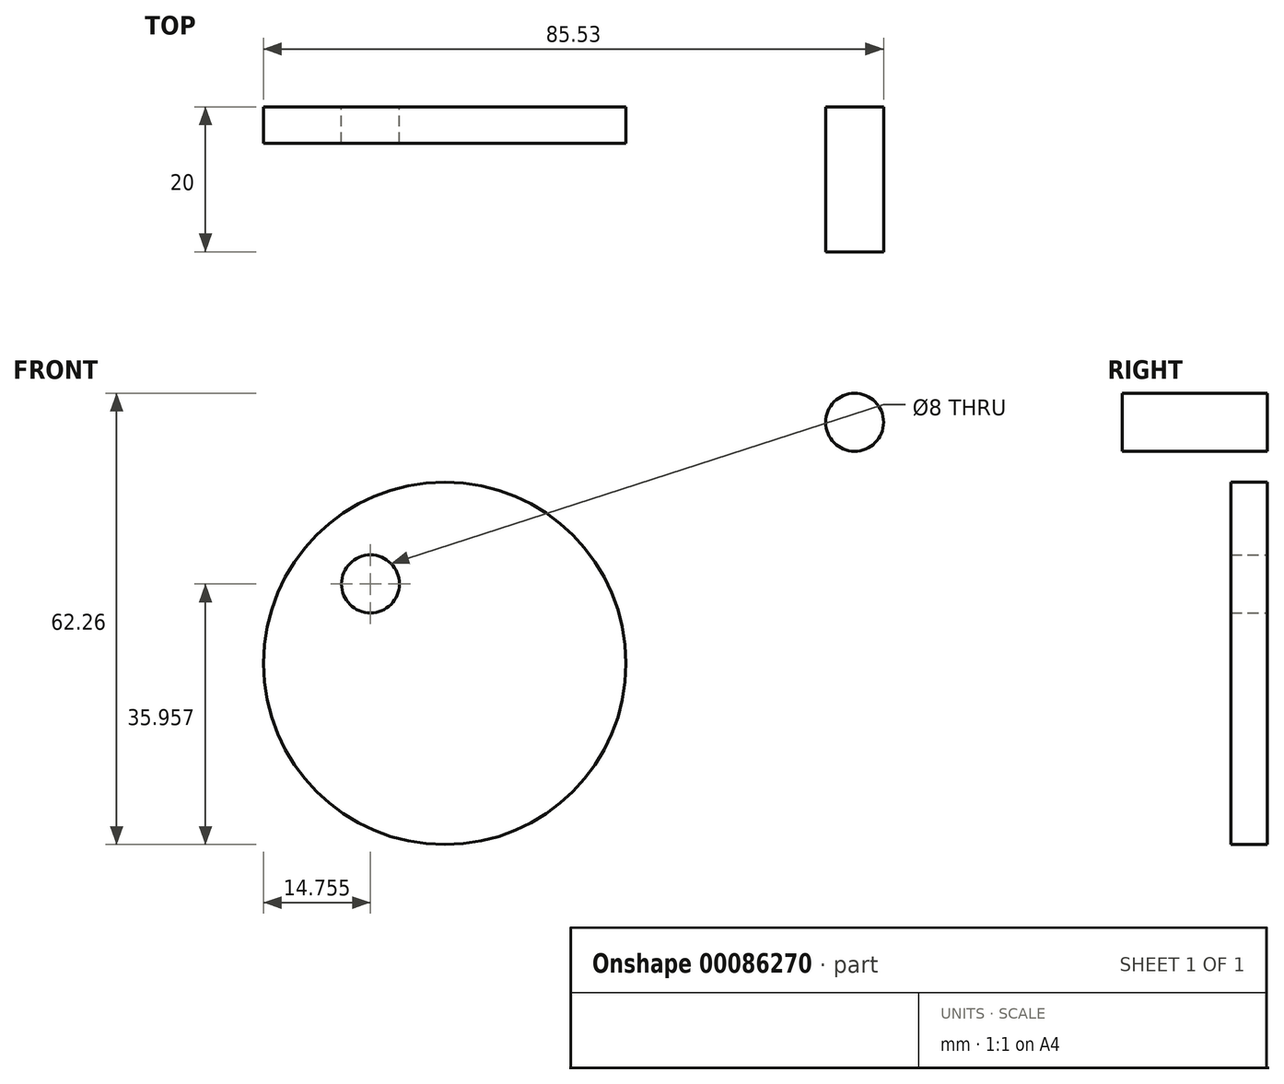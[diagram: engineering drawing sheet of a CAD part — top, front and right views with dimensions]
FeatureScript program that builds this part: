
annotation { "Feature Type Name" : "Feature", "Feature Type Description" : "" }
export const myFeature = defineFeature(function(context is Context, id is Id, definition is map)
    precondition{}
    {
        {
            var Q0;
            Q0=qCreatedBy(makeId("Front.planeOp"),FACE);
            var sketch = newSketch(context, id + "F0", { "sketchPlane" : qUnion([Q0])});
            skCircle(sketch, "E0", {"center": v(0, 0) * mm, "radius": 25 * mm});
            skCircle(sketch, "E1", {"center": v(-10.24, 10.96) * mm, "radius": 4 * mm});
            skSolve(sketch);
        }
        {
            var Q0;
            Q0=makeQuery(id+"F0.imprint","IMPRINT",FACE,{"disambiguationData":[TD([[makeQuery(id+"F0.imprint","IMPRINT",EDGE,{"derivedFrom":sQuery(id+"F0.wireOp",EDGE,"E0")}),1.0]])]});
            extrude(context, id + "F1", {"entities" : qUnion([Q0]), "depth" : 5 * mm});
        }
        {
            var Q0;
            Q0=qCreatedBy(makeId("Front.planeOp"),FACE);
            var sketch = newSketch(context, id + "F2", { "sketchPlane" : qUnion([Q0])});
            skCircle(sketch, "E2", {"center": v(56.53, 33.26) * mm, "radius": 4 * mm});
            skSolve(sketch);
        }
        {
            var Q0;
            Q0=makeQuery(id+"F2.imprint","IMPRINT",FACE,{"disambiguationData":[TD([[makeQuery(id+"F2.imprint","IMPRINT",EDGE,{"derivedFrom":sQuery(id+"F2.wireOp",EDGE,"E2")}),1.0]])]});
            extrude(context, id + "F3", {"entities" : qUnion([Q0]), "depth" : 20 * mm});
        }
    });
